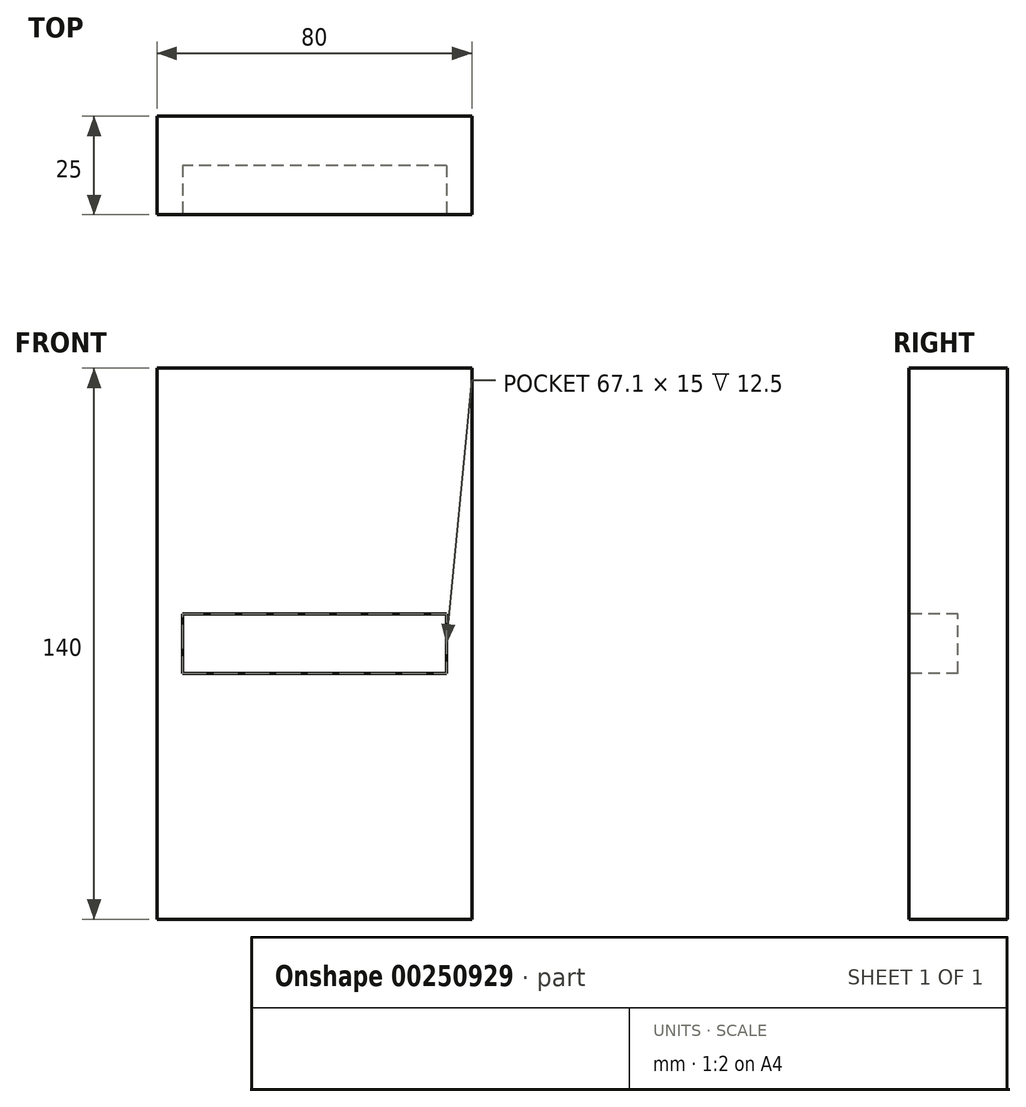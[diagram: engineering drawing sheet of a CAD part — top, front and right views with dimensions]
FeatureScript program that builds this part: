
annotation { "Feature Type Name" : "Feature", "Feature Type Description" : "" }
export const myFeature = defineFeature(function(context is Context, id is Id, definition is map)
    precondition{}
    {
        {
            var Q0;
            Q0=qCreatedBy(makeId("Front.planeOp"),FACE);
            var sketch = newSketch(context, id + "F0", { "sketchPlane" : qUnion([Q0])});
            skLineSegment(sketch, "E0.bottom", {"start": v(40, -70) * mm, "end": v(-40, -70) * mm});
            skLineSegment(sketch, "E0.top", {"start": v(40, 70) * mm, "end": v(-40, 70) * mm});
            skLineSegment(sketch, "E0.left", {"start": v(40, -70) * mm, "end": v(40, 70) * mm});
            skLineSegment(sketch, "E0.right", {"start": v(-40, -70) * mm, "end": v(-40, 70) * mm});
            skPoint(sketch, "E0.middle", {"position": v(0, 0) * mm});
            skSolve(sketch);
        }
        {
            var Q0;
            Q0=makeQuery(id+"F0.imprint","IMPRINT",FACE,{"disambiguationData":[TD([[makeQuery(id+"F0.imprint","IMPRINT",EDGE,{"derivedFrom":sQuery(id+"F0.wireOp",EDGE,"E0.bottom")}),-1.0]])]});
            extrude(context, id + "F1", {"entities" : qUnion([Q0]), "endBound" : BoundingType.SYMMETRIC, "depth" : 25 * mm});
        }
        {
            var Q0;
            Q0=makeQuery(id+"F1.opExtrude","CAP_FACE",FACE,{"disambiguationData":[OSD([sQuery(id+"F0.wireOp",EDGE,"E0.bottom"),sQuery(id+"F0.wireOp",EDGE,"E0.top"),sQuery(id+"F0.wireOp",EDGE,"E0.left"),sQuery(id+"F0.wireOp",EDGE,"E0.right")])],"isStart":false});
            var sketch = newSketch(context, id + "F2", { "sketchPlane" : qUnion([Q0])});
            skLineSegment(sketch, "E1.bottom", {"start": v(33.55, -7.5) * mm, "end": v(-33.55, -7.5) * mm});
            skLineSegment(sketch, "E1.top", {"start": v(33.55, 7.5) * mm, "end": v(-33.55, 7.5) * mm});
            skLineSegment(sketch, "E1.left", {"start": v(33.55, -7.5) * mm, "end": v(33.55, 7.5) * mm});
            skLineSegment(sketch, "E1.right", {"start": v(-33.55, -7.5) * mm, "end": v(-33.55, 7.5) * mm});
            skPoint(sketch, "E1.middle", {"position": v(0, 0) * mm});
            skSolve(sketch);
        }
        {
            var Q0;
            Q0=makeQuery(id+"F2.imprint","IMPRINT",FACE,{"disambiguationData":[TD([[makeQuery(id+"F2.imprint","IMPRINT",EDGE,{"derivedFrom":sQuery(id+"F2.wireOp",EDGE,"E1.bottom")}),-1.0]])]});
            extrude(context, id + "F3", {"entities" : qUnion([Q0]), "operationType" : NewBodyOperationType.REMOVE, "endBound" : BoundingType.SYMMETRIC, "oppositeDirection" : true, "depth" : 25 * mm});
        }
    });
